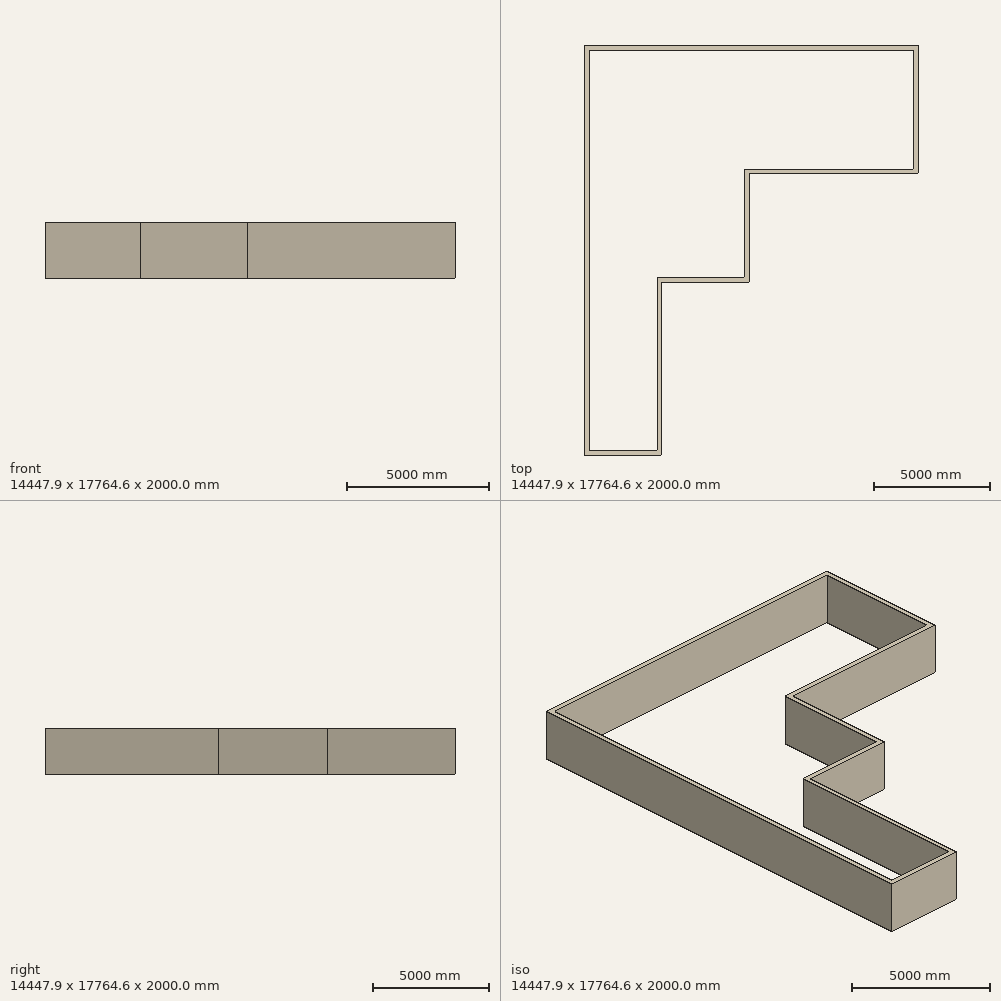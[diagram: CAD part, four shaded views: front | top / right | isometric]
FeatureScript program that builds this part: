
annotation { "Feature Type Name" : "Feature", "Feature Type Description" : "" }
export const myFeature = defineFeature(function(context is Context, id is Id, definition is map)
    precondition{}
    {
        {
            var Q0;
            Q0=qCreatedBy(makeId("Top.planeOp"),FACE);
            var sketch = newSketch(context, id + "F0", { "sketchPlane" : qUnion([Q0])});
            skLineSegment(sketch, "E0.bottom", {"start": v(-12481.58, 5303.98) * mm, "end": v(1766.33, 5303.98) * mm});
            skLineSegment(sketch, "E0.top", {"start": v(-12481.58, 5103.98) * mm, "end": v(1766.33, 5103.98) * mm});
            skLineSegment(sketch, "E0.left", {"start": v(-12481.58, 5303.98) * mm, "end": v(-12481.58, 5103.98) * mm});
            skLineSegment(sketch, "E0.right", {"start": v(1766.33, 5303.98) * mm, "end": v(1766.33, 5103.98) * mm});
            skLineSegment(sketch, "E1.bottom", {"start": v(1766.33, 5103.98) * mm, "end": v(1566.33, 5103.98) * mm});
            skLineSegment(sketch, "E1.top", {"start": v(1766.33, -256.02) * mm, "end": v(1566.33, -256.02) * mm});
            skLineSegment(sketch, "E1.left", {"start": v(1766.33, 5103.98) * mm, "end": v(1766.33, -256.02) * mm});
            skLineSegment(sketch, "E1.right", {"start": v(1566.33, 5103.98) * mm, "end": v(1566.33, -256.02) * mm});
            skLineSegment(sketch, "E2.bottom", {"start": v(1566.33, -256.02) * mm, "end": v(-5553.67, -256.02) * mm});
            skLineSegment(sketch, "E2.top", {"start": v(1566.33, -56.02) * mm, "end": v(-5553.67, -56.02) * mm});
            skLineSegment(sketch, "E2.left", {"start": v(1566.33, -256.02) * mm, "end": v(1566.33, -56.02) * mm});
            skLineSegment(sketch, "E2.right", {"start": v(-5553.67, -256.02) * mm, "end": v(-5553.67, -56.02) * mm});
            skLineSegment(sketch, "E3.bottom", {"start": v(-5553.67, -56.02) * mm, "end": v(-5753.67, -56.02) * mm});
            skLineSegment(sketch, "E3.top", {"start": v(-5553.67, -4964.77) * mm, "end": v(-5753.67, -4964.77) * mm});
            skLineSegment(sketch, "E3.left", {"start": v(-5553.67, -56.02) * mm, "end": v(-5553.67, -4964.77) * mm});
            skLineSegment(sketch, "E3.right", {"start": v(-5753.67, -56.02) * mm, "end": v(-5753.67, -4964.77) * mm});
            skLineSegment(sketch, "E4.bottom", {"start": v(-5753.67, -4964.77) * mm, "end": v(-9344.62, -4964.77) * mm});
            skLineSegment(sketch, "E4.top", {"start": v(-5753.67, -4764.77) * mm, "end": v(-9344.62, -4764.77) * mm});
            skLineSegment(sketch, "E4.left", {"start": v(-5753.67, -4964.77) * mm, "end": v(-5753.67, -4764.77) * mm});
            skLineSegment(sketch, "E4.right", {"start": v(-9344.62, -4964.77) * mm, "end": v(-9344.62, -4764.77) * mm});
            skLineSegment(sketch, "E5.bottom", {"start": v(-9344.62, -4764.77) * mm, "end": v(-9544.62, -4764.77) * mm});
            skLineSegment(sketch, "E5.top", {"start": v(-9344.62, -12260.6) * mm, "end": v(-9544.62, -12260.6) * mm});
            skLineSegment(sketch, "E5.left", {"start": v(-9344.62, -4764.77) * mm, "end": v(-9344.62, -12260.6) * mm});
            skLineSegment(sketch, "E5.right", {"start": v(-9544.62, -4764.77) * mm, "end": v(-9544.62, -12260.6) * mm});
            skLineSegment(sketch, "E6.bottom", {"start": v(-12481.58, 5303.98) * mm, "end": v(-12681.58, 5303.98) * mm});
            skLineSegment(sketch, "E6.top", {"start": v(-12481.58, -12260.6) * mm, "end": v(-12681.58, -12260.6) * mm});
            skLineSegment(sketch, "E6.left", {"start": v(-12481.58, 5303.98) * mm, "end": v(-12481.58, -12260.6) * mm});
            skLineSegment(sketch, "E6.right", {"start": v(-12681.58, 5303.98) * mm, "end": v(-12681.58, -12260.6) * mm});
            skLineSegment(sketch, "E7.bottom", {"start": v(-12681.58, -12260.6) * mm, "end": v(-9344.62, -12260.6) * mm});
            skLineSegment(sketch, "E7.top", {"start": v(-12681.58, -12460.6) * mm, "end": v(-9344.62, -12460.6) * mm});
            skLineSegment(sketch, "E7.left", {"start": v(-12681.58, -12260.6) * mm, "end": v(-12681.58, -12460.6) * mm});
            skLineSegment(sketch, "E7.right", {"start": v(-9344.62, -12260.6) * mm, "end": v(-9344.62, -12460.6) * mm});
            skSolve(sketch);
        }
        {
            var Q0;
            Q0 = qSketchRegion(id + "F0", true);
            extrude(context, id + "F1", {"entities" : qUnion([Q0]), "depth" : 2000 * mm, "offsetDistance" : 25 * mm});
        }
    });
